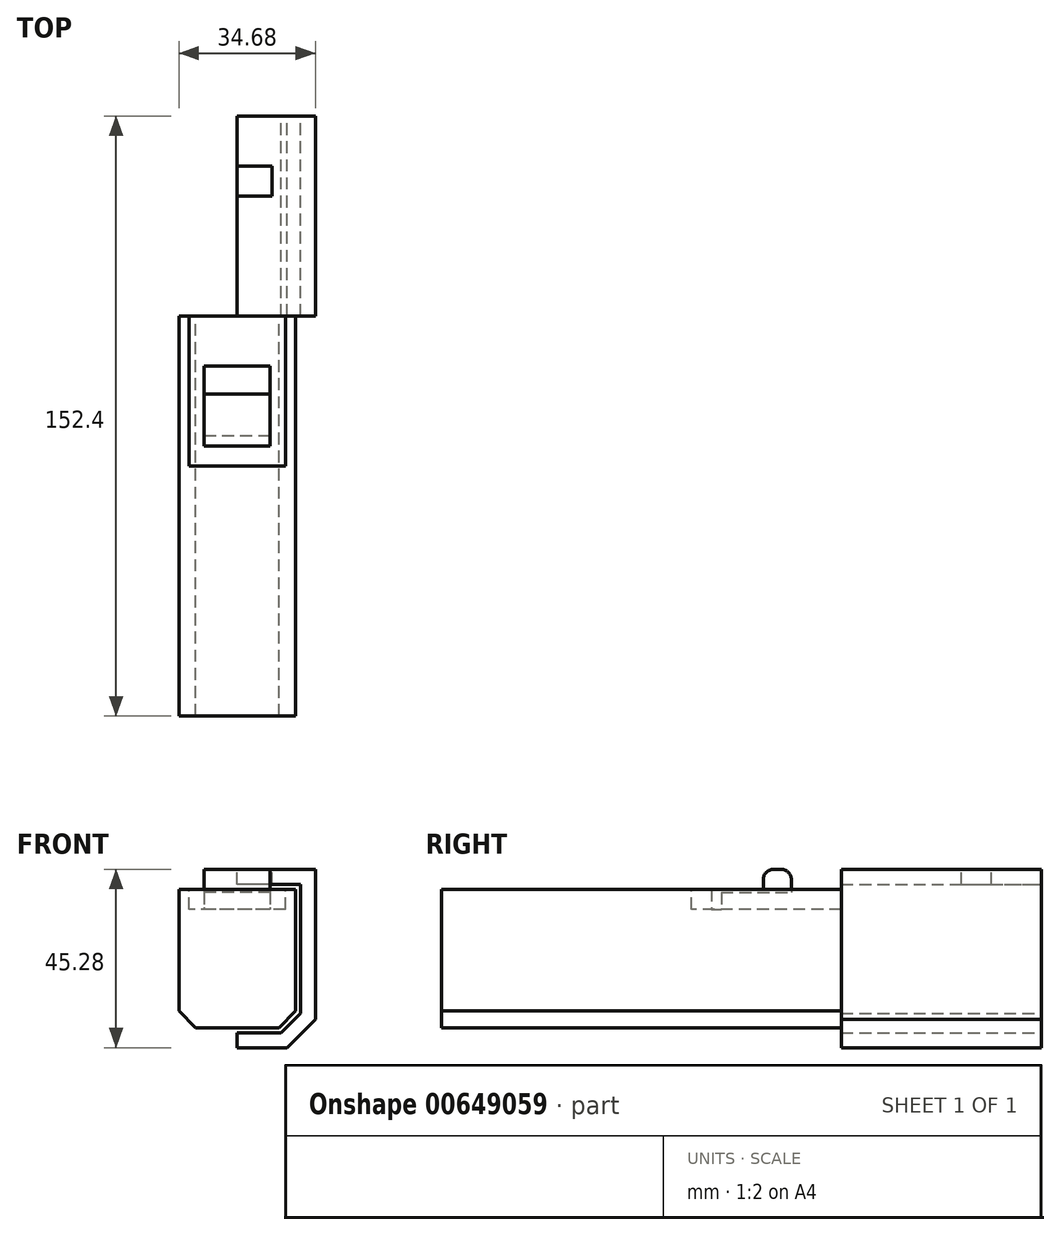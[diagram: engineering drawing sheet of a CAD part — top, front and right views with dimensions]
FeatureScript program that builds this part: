
annotation { "Feature Type Name" : "Feature", "Feature Type Description" : "" }
export const myFeature = defineFeature(function(context is Context, id is Id, definition is map)
    precondition{}
    {
        {
            var Q0;
            Q0=qCreatedBy(makeId("Front.planeOp"),FACE);
            var sketch = newSketch(context, id + "F0", { "sketchPlane" : qUnion([Q0])});
            skLineSegment(sketch, "E0", {"start": v(0, 0) * mm, "end": v(12.7, 0) * mm});
            skLineSegment(sketch, "E1", {"start": v(12.7, 0) * mm, "end": v(19.88, 7.18) * mm});
            skLineSegment(sketch, "E2", {"start": v(19.88, 7.18) * mm, "end": v(19.88, 45.28) * mm});
            skLineSegment(sketch, "E3", {"start": v(19.88, 45.28) * mm, "end": v(0, 45.28) * mm});
            skLineSegment(sketch, "E4", {"start": v(0, 45.28) * mm, "end": v(0, 0) * mm});
            skLineSegment(sketch, "E5", {"start": v(16.07, 41.47) * mm, "end": v(16.07, 11.27) * mm});
            skLineSegment(sketch, "E6", {"start": v(13.6, 6.29) * mm, "end": v(16.07, 8.76) * mm});
            skLineSegment(sketch, "E7", {"start": v(16.07, 8.76) * mm, "end": v(16.07, 11.27) * mm});
            skLineSegment(sketch, "E8", {"start": v(13.6, 6.29) * mm, "end": v(11.12, 3.8) * mm});
            skLineSegment(sketch, "E9", {"start": v(11.12, 3.81) * mm, "end": v(0, 3.81) * mm});
            skLineSegment(sketch, "E10", {"start": v(16.07, 41.47) * mm, "end": v(0, 41.47) * mm});
            skLineSegment(sketch, "E11", {"start": v(0, 45.28) * mm, "end": v(0, 41.47) * mm});
            skLineSegment(sketch, "E12", {"start": v(16.07, 41.47) * mm, "end": v(16.07, 45.28) * mm, "construction": true});
            skLineSegment(sketch, "E13.MirrorCS", {"start": v(-16.07, 41.47) * mm, "end": v(0, 41.47) * mm});
            skLineSegment(sketch, "E14.MirrorCS", {"start": v(-19.88, 45.28) * mm, "end": v(0, 45.28) * mm});
            skLineSegment(sketch, "E15.MirrorCS", {"start": v(-16.07, 41.47) * mm, "end": v(-16.07, 45.28) * mm, "construction": true});
            skLineSegment(sketch, "E16.MirrorCS", {"start": v(-16.07, 41.47) * mm, "end": v(-16.07, 11.27) * mm});
            skLineSegment(sketch, "E17.MirrorCS", {"start": v(-19.88, 7.18) * mm, "end": v(-19.88, 45.28) * mm});
            skLineSegment(sketch, "E18.MirrorCS", {"start": v(-12.7, 0) * mm, "end": v(-19.88, 7.18) * mm});
            skLineSegment(sketch, "E19.MirrorCS", {"start": v(-13.6, 6.29) * mm, "end": v(-16.07, 8.76) * mm});
            skLineSegment(sketch, "E20.MirrorCS", {"start": v(-13.6, 6.29) * mm, "end": v(-11.12, 3.8) * mm});
            skLineSegment(sketch, "E21.MirrorCS", {"start": v(-16.07, 8.76) * mm, "end": v(-16.07, 11.27) * mm});
            skLineSegment(sketch, "E22.MirrorCS", {"start": v(-11.12, 3.81) * mm, "end": v(0, 3.81) * mm});
            skLineSegment(sketch, "E23.MirrorCS", {"start": v(0, 0) * mm, "end": v(-12.7, 0) * mm});
            skSolve(sketch);
        }
        {
            var Q0;
            Q0=makeQuery(id+"F0.imprint","IMPRINT",FACE,{"disambiguationData":[TD([[makeQuery(id+"F0.imprint","IMPRINT",EDGE,{"derivedFrom":sQuery(id+"F0.wireOp",EDGE,"E11")}),-1.0]])]});
            var Q1;
            {var subQ2=sQuery(id+"F0.wireOp",EDGE,"E0");Q1=makeQuery(id+"F0.imprint","IMPRINT",FACE,{"disambiguationData":[TD([[makeQuery(id+"F0.imprint","IMPRINT",EDGE,{"derivedFrom":subQ2}),1.0]])]});}
            extrude(context, id + "F1", {"entities" : qUnion([Q0, Q1]), "depth" : 50.8 * mm, "offsetDistance" : 25.4 * mm});
        }
        {
            var Q0;
            Q0=makeQuery(id+"F1.opExtrude","CAP_FACE",FACE,{"disambiguationData":[OSD([sQuery(id+"F0.wireOp",EDGE,"E0"),sQuery(id+"F0.wireOp",EDGE,"E1"),sQuery(id+"F0.wireOp",EDGE,"E2"),sQuery(id+"F0.wireOp",EDGE,"E3"),sQuery(id+"F0.wireOp",EDGE,"E5"),sQuery(id+"F0.wireOp",EDGE,"E6"),sQuery(id+"F0.wireOp",EDGE,"E7"),sQuery(id+"F0.wireOp",EDGE,"E8"),sQuery(id+"F0.wireOp",EDGE,"E9"),sQuery(id+"F0.wireOp",EDGE,"E10"),sQuery(id+"F0.wireOp",EDGE,"E13.MirrorCS"),sQuery(id+"F0.wireOp",EDGE,"E14.MirrorCS"),sQuery(id+"F0.wireOp",EDGE,"E16.MirrorCS"),sQuery(id+"F0.wireOp",EDGE,"E17.MirrorCS"),sQuery(id+"F0.wireOp",EDGE,"E18.MirrorCS"),sQuery(id+"F0.wireOp",EDGE,"E19.MirrorCS"),sQuery(id+"F0.wireOp",EDGE,"E20.MirrorCS"),sQuery(id+"F0.wireOp",EDGE,"E21.MirrorCS"),sQuery(id+"F0.wireOp",EDGE,"E22.MirrorCS"),sQuery(id+"F0.wireOp",EDGE,"E23.MirrorCS")])],"isStart":false});
            var sketch = newSketch(context, id + "F2", { "sketchPlane" : qUnion([Q0])});
            skLineSegment(sketch, "E24", {"start": v(0, 0) * mm, "end": v(0, 5.08) * mm, "construction": true});
            skLineSegment(sketch, "E25", {"start": v(12.7, 0) * mm, "end": v(11.12, 3.8) * mm, "construction": true});
            skLineSegment(sketch, "E26", {"start": v(11.12, 3.8) * mm, "end": v(10.6, 5.08) * mm, "construction": true});
            skLineSegment(sketch, "E27", {"start": v(0, 5.08) * mm, "end": v(10.6, 5.08) * mm});
            skLineSegment(sketch, "E28", {"start": v(19.88, 7.18) * mm, "end": v(16.07, 8.76) * mm});
            skLineSegment(sketch, "E29", {"start": v(16.07, 8.76) * mm, "end": v(14.8, 9.29) * mm});
            skLineSegment(sketch, "E30", {"start": v(10.6, 5.08) * mm, "end": v(14.8, 9.29) * mm});
            skLineSegment(sketch, "E31", {"start": v(4.4, 45.28) * mm, "end": v(4.4, 40.2) * mm, "construction": true});
            skLineSegment(sketch, "E32", {"start": v(0, 5.08) * mm, "end": v(0, 40.2) * mm});
            skLineSegment(sketch, "E33", {"start": v(0, 40.2) * mm, "end": v(4.4, 40.2) * mm});
            skLineSegment(sketch, "E34", {"start": v(14.8, 40.2) * mm, "end": v(14.8, 9.29) * mm});
            skLineSegment(sketch, "E35", {"start": v(14.8, 40.2) * mm, "end": v(4.4, 40.2) * mm});
            skLineSegment(sketch, "E36.MirrorCS", {"start": v(0, 40.2) * mm, "end": v(-4.4, 40.2) * mm});
            skLineSegment(sketch, "E37.MirrorCS", {"start": v(-14.8, 40.2) * mm, "end": v(-4.4, 40.2) * mm});
            skLineSegment(sketch, "E38.MirrorCS", {"start": v(-14.8, 40.2) * mm, "end": v(-14.8, 9.29) * mm});
            skLineSegment(sketch, "E39.MirrorCS", {"start": v(-10.6, 5.08) * mm, "end": v(-14.8, 9.29) * mm});
            skLineSegment(sketch, "E40.MirrorCS", {"start": v(0, 5.08) * mm, "end": v(-10.6, 5.08) * mm});
            skSolve(sketch);
        }
        {
            var Q0;
            Q0=makeQuery(id+"F2.imprint","IMPRINT",FACE,{"disambiguationData":[TD([[makeQuery(id+"F2.imprint","IMPRINT",EDGE,{"derivedFrom":sQuery(id+"F2.wireOp",EDGE,"E27")}),1.0]])]});
            var Q1;
            Q1=makeQuery(id+"F2.imprint","IMPRINT",FACE,{"disambiguationData":[TD([[makeQuery(id+"F2.imprint","IMPRINT",EDGE,{"derivedFrom":sQuery(id+"F2.wireOp",EDGE,"E32")}),1.0]])]});
            extrude(context, id + "F3", {"entities" : qUnion([Q0, Q1]), "depth" : 101.6 * mm, "offsetDistance" : 25.4 * mm});
        }
        {
            var Q0;
            Q0=makeQuery(id+"F1.opExtrude","SWEPT_FACE",FACE,{"disambiguationData":[OSD([sQuery(id+"F0.wireOp",EDGE,"E3"),sQuery(id+"F0.wireOp",EDGE,"E14.MirrorCS")])]});
            var sketch = newSketch(context, id + "F4", { "sketchPlane" : qUnion([Q0])});
            skLineSegment(sketch, "E41", {"start": v(0, 0) * mm, "end": v(0, -12.7) * mm, "construction": true});
            skLineSegment(sketch, "E42", {"start": v(0, -12.7) * mm, "end": v(8.9, -12.7) * mm});
            skLineSegment(sketch, "E43", {"start": v(8.9, -12.7) * mm, "end": v(8.9, -20.32) * mm});
            skLineSegment(sketch, "E44", {"start": v(8.9, -20.32) * mm, "end": v(0, -20.32) * mm});
            skLineSegment(sketch, "E45.MirrorCS", {"start": v(0, -12.7) * mm, "end": v(-8.9, -12.7) * mm});
            skLineSegment(sketch, "E46.MirrorCS", {"start": v(-8.9, -12.7) * mm, "end": v(-8.9, -20.32) * mm});
            skLineSegment(sketch, "E47.MirrorCS", {"start": v(-8.9, -20.32) * mm, "end": v(0, -20.32) * mm});
            skSolve(sketch);
        }
        {
            var Q0;
            Q0=makeQuery(id+"F4.imprint","IMPRINT",FACE,{"disambiguationData":[TD([[makeQuery(id+"F4.imprint","IMPRINT",EDGE,{"derivedFrom":sQuery(id+"F4.wireOp",EDGE,"E42")}),-1.0]])]});
            extrude(context, id + "F5", {"entities" : qUnion([Q0]), "operationType" : NewBodyOperationType.REMOVE, "oppositeDirection" : true, "depth" : 25.4 * mm, "offsetDistance" : 25.4 * mm});
        }
        {
            var Q0;
            Q0=makeQuery(id+"F3.opExtrude","SWEPT_FACE",FACE,{"disambiguationData":[OSD([sQuery(id+"F2.wireOp",EDGE,"E33"),sQuery(id+"F2.wireOp",EDGE,"E35"),sQuery(id+"F2.wireOp",EDGE,"E36.MirrorCS"),sQuery(id+"F2.wireOp",EDGE,"E37.MirrorCS")])]});
            var sketch = newSketch(context, id + "F6", { "sketchPlane" : qUnion([Q0])});
            skLineSegment(sketch, "E48", {"start": v(-14.8, -50.8) * mm, "end": v(-12.26, -50.8) * mm, "construction": true});
            skLineSegment(sketch, "E49", {"start": v(-12.26, -50.8) * mm, "end": v(-12.26, -88.9) * mm});
            skLineSegment(sketch, "E50", {"start": v(0, -51.45) * mm, "end": v(-12.26, -51.45) * mm, "construction": true});
            skPoint(sketch, "E50.startSnap0", {"position": v(0, -50.8) * mm});
            skLineSegment(sketch, "E51", {"start": v(0, -51.45) * mm, "end": v(0, -77.88) * mm, "construction": true});
            skLineSegment(sketch, "E52", {"start": v(-12.26, -88.9) * mm, "end": v(0, -88.9) * mm});
            skLineSegment(sketch, "E53.MirrorCS", {"start": v(0, -51.45) * mm, "end": v(12.26, -51.45) * mm, "construction": true});
            skLineSegment(sketch, "E54.MirrorCS", {"start": v(12.26, -88.9) * mm, "end": v(0, -88.9) * mm});
            skLineSegment(sketch, "E55.MirrorCS", {"start": v(12.26, -50.8) * mm, "end": v(12.26, -88.9) * mm});
            skSolve(sketch);
        }
        {
            var Q0;
            {var subQ1=sQuery(id+"F6.wireOp",EDGE,"E49");Q0=makeQuery(id+"F6.imprint","IMPRINT",FACE,{"disambiguationData":[TD([[makeQuery(id+"F6.imprint","IMPRINT",EDGE,{"derivedFrom":subQ1}),1.0]])]});}
            extrude(context, id + "F7", {"entities" : qUnion([Q0]), "operationType" : NewBodyOperationType.REMOVE, "oppositeDirection" : true, "depth" : 5.08 * mm, "offsetDistance" : 25.4 * mm});
        }
        {
            var Q0;
            Q0=makeQuery(id+"F7.boolean.opBoolean","COPY",FACE,{"derivedFrom":makeQuery(id+"F7.opExtrude","CAP_FACE",FACE,{"disambiguationData":[OSD([sQuery(id+"F2.wireOp",EDGE,"E33"),sQuery(id+"F2.wireOp",EDGE,"E35"),sQuery(id+"F2.wireOp",EDGE,"E36.MirrorCS"),sQuery(id+"F2.wireOp",EDGE,"E37.MirrorCS"),sQuery(id+"F6.wireOp",EDGE,"E49"),sQuery(id+"F6.wireOp",EDGE,"E52"),sQuery(id+"F6.wireOp",EDGE,"E54.MirrorCS"),sQuery(id+"F6.wireOp",EDGE,"E55.MirrorCS")])],"isStart":false})});
            var sketch = newSketch(context, id + "F8", { "sketchPlane" : qUnion([Q0])});
            skLineSegment(sketch, "E56", {"start": v(0, -88.9) * mm, "end": v(0, -83.82) * mm});
            skLineSegment(sketch, "E57", {"start": v(0, -83.82) * mm, "end": v(8.38, -83.82) * mm});
            skLineSegment(sketch, "E58", {"start": v(8.38, -83.82) * mm, "end": v(8.38, -81.28) * mm});
            skLineSegment(sketch, "E59", {"start": v(8.38, -81.28) * mm, "end": v(0, -81.28) * mm});
            skLineSegment(sketch, "E60.MirrorCS", {"start": v(0, -83.82) * mm, "end": v(-8.38, -83.82) * mm});
            skLineSegment(sketch, "E61.MirrorCS", {"start": v(-8.38, -83.82) * mm, "end": v(-8.38, -81.28) * mm});
            skLineSegment(sketch, "E62.MirrorCS", {"start": v(-8.38, -81.28) * mm, "end": v(0, -81.28) * mm});
            skLineSegment(sketch, "E63", {"start": v(0, -50.8) * mm, "end": v(0, -81.28) * mm, "construction": true});
            skSolve(sketch);
        }
        {
            var Q0;
            Q0 = qSketchRegion(id + "F8", true);
            extrude(context, id + "F9", {"entities" : qUnion([Q0]), "operationType" : NewBodyOperationType.ADD, "depth" : 4.32 * mm, "offsetDistance" : 25.4 * mm});
        }
        {
            var Q0;
            Q0=makeQuery(id+"F9.opExtrude","CAP_FACE",FACE,{"disambiguationData":[OSD([sQuery(id+"F8.wireOp",EDGE,"E57"),sQuery(id+"F8.wireOp",EDGE,"E58"),sQuery(id+"F8.wireOp",EDGE,"E59"),sQuery(id+"F8.wireOp",EDGE,"E60.MirrorCS"),sQuery(id+"F8.wireOp",EDGE,"E61.MirrorCS"),sQuery(id+"F8.wireOp",EDGE,"E62.MirrorCS")])],"isStart":false});
            var sketch = newSketch(context, id + "F10", { "sketchPlane" : qUnion([Q0])});
            skPoint(sketch, "E64.oppositeSnap0", {"position": v(0, -81.28) * mm});
            skLineSegment(sketch, "E64.bottom", {"start": v(-8.38, -83.82) * mm, "end": v(0, -83.82) * mm});
            skLineSegment(sketch, "E64.top", {"start": v(-8.38, -63.5) * mm, "end": v(0, -63.5) * mm});
            skLineSegment(sketch, "E64.left", {"start": v(-8.38, -83.82) * mm, "end": v(-8.38, -63.5) * mm});
            skLineSegment(sketch, "E64.right", {"start": v(0, -83.82) * mm, "end": v(0, -63.5) * mm});
            skLineSegment(sketch, "E65.MirrorCS", {"start": v(8.38, -83.82) * mm, "end": v(8.38, -63.5) * mm});
            skLineSegment(sketch, "E66.MirrorCS", {"start": v(8.38, -63.5) * mm, "end": v(0, -63.5) * mm});
            skSolve(sketch);
        }
        {
            var Q0;
            {var subQ0=sQuery(id+"F10.wireOp",EDGE,"E64.top");Q0=makeQuery(id+"F10.imprint","IMPRINT",FACE,{"disambiguationData":[TD([[makeQuery(id+"F10.imprint","IMPRINT",EDGE,{"derivedFrom":subQ0}),-1.0]])]});}
            var Q1;
            {var subQ0=sQuery(id+"F10.wireOp",EDGE,"E66.MirrorCS");Q1=makeQuery(id+"F10.imprint","IMPRINT",FACE,{"disambiguationData":[TD([[makeQuery(id+"F10.imprint","IMPRINT",EDGE,{"derivedFrom":subQ0}),1.0]])]});}
            var Q2;
            {var subQ1=makeQuery(id+"F9.opExtrude","CAP_EDGE",EDGE,{"disambiguationData":[OSD([sQuery(id+"F8.wireOp",EDGE,"E57"),sQuery(id+"F8.wireOp",EDGE,"E60.MirrorCS")])],"isStart":false});var subQ5=sQuery(id+"F10.wireOp",EDGE,"E65.MirrorCS");var subQ6=makeQuery(id+"F10.imprint","INTERSECT",VERTEX,{"derivedFrom":[subQ1,subQ5]});Q2=makeQuery(id+"F10.imprint","IMPRINT",FACE,{"disambiguationData":[TD([[makeQuery(id+"F10.imprint","IMPRINT",EDGE,{"disambiguationData":[TD([[subQ6,-1.0]])],"derivedFrom":subQ5}),1.0]])]});}
            var Q3;
            {var subQ0=sQuery(id+"F10.wireOp",EDGE,"E64.bottom");Q3=makeQuery(id+"F10.imprint","IMPRINT",FACE,{"disambiguationData":[TD([[makeQuery(id+"F10.imprint","IMPRINT",EDGE,{"derivedFrom":subQ0}),-1.0]])]});}
            extrude(context, id + "F11", {"entities" : qUnion([Q0, Q1, Q2, Q3]), "operationType" : NewBodyOperationType.ADD, "depth" : 0.76 * mm, "offsetDistance" : 25.4 * mm});
        }
        {
            var Q0;
            Q0=makeQuery(id+"F11.opExtrude","CAP_FACE",FACE,{"disambiguationData":[OSD([sQuery(id+"F8.wireOp",EDGE,"E57"),sQuery(id+"F8.wireOp",EDGE,"E60.MirrorCS"),sQuery(id+"F10.wireOp",EDGE,"E64.bottom"),sQuery(id+"F10.wireOp",EDGE,"E64.top"),sQuery(id+"F10.wireOp",EDGE,"E64.left"),sQuery(id+"F10.wireOp",EDGE,"E65.MirrorCS"),sQuery(id+"F10.wireOp",EDGE,"E66.MirrorCS")])],"isStart":false});
            var sketch = newSketch(context, id + "F12", { "sketchPlane" : qUnion([Q0])});
            skLineSegment(sketch, "E67", {"start": v(-8.38, -63.5) * mm, "end": v(-8.38, -70.61) * mm});
            skLineSegment(sketch, "E68", {"start": v(8.38, -70.61) * mm, "end": v(-8.38, -70.61) * mm});
            skLineSegment(sketch, "E69", {"start": v(8.38, -70.61) * mm, "end": v(8.38, -63.5) * mm});
            skLineSegment(sketch, "E70", {"start": v(8.38, -63.5) * mm, "end": v(-8.38, -63.5) * mm});
            skSolve(sketch);
        }
        {
            var Q0;
            Q0=makeQuery(id+"F12.imprint","IMPRINT",FACE,{"disambiguationData":[TD([[makeQuery(id+"F12.imprint","IMPRINT",EDGE,{"derivedFrom":sQuery(id+"F12.wireOp",EDGE,"E67")}),-1.0]])]});
            extrude(context, id + "F13", {"entities" : qUnion([Q0]), "operationType" : NewBodyOperationType.ADD, "depth" : 5.08 * mm, "offsetDistance" : 25.4 * mm});
        }
        {
            var Q0;
            Q0=makeQuery(id+"F13.opExtrude","CAP_EDGE",EDGE,{"disambiguationData":[OSD([sQuery(id+"F12.wireOp",EDGE,"E70")])],"isStart":false});
            var Q1;
            Q1=makeQuery(id+"F13.opExtrude","CAP_EDGE",EDGE,{"disambiguationData":[OSD([sQuery(id+"F12.wireOp",EDGE,"E68")])],"isStart":false});
            fillet(context, id + "F14", {"entities" : qUnion([Q0, Q1]), "radius" : 2.54 * mm, "tangentPropagation" : true, "allowEdgeOverflow" : false});
        }
    });
